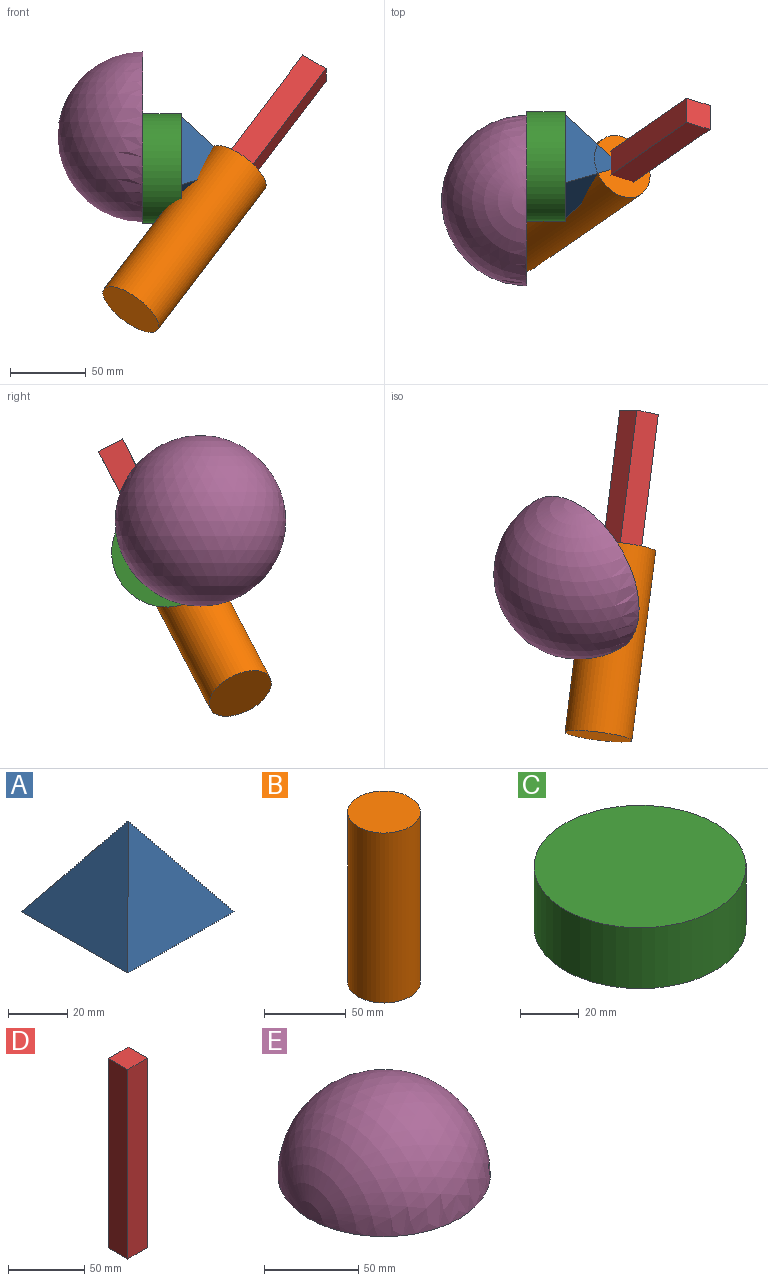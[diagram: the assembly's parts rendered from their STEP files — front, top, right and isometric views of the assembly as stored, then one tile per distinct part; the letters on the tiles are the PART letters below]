
ASSEMBLY  parts=5 mates=4
PART A: 5 faces, bbox 50.8x50.8x37.7 mm
  f0: plane 50.8x37.66mm, normal (-0.83,0,0.56), area 1153.7mm2, adj f1,f2,f3
  f1: plane 50.8x50.8mm, normal (0,0,-1), area 2580.6mm2, adj f0,f2,f3,f4
  f2: plane 50.8x37.66mm, normal (0,-0.83,0.56), area 1153.7mm2, adj f0,f1,f4
  f3: plane 50.8x37.66mm, normal (0,0.83,0.56), area 1153.7mm2, adj f0,f1,f4
  f4: plane 50.8x37.66mm, normal (0.83,0,0.56), area 1153.7mm2, adj f1,f2,f3
PART B: 3 faces, bbox 44.5x44.5x127 mm
  f0: cylinder r=22.26mm len=127mm, axis (0,0,-1), area 17763mm2, adj f1,f2
  f1: plane 44.52x44.52mm, normal (0,0,1), area 1556.7mm2, adj f0
  f2: plane 44.52x44.52mm, normal (0,0,-1), area 1556.7mm2, adj f0
PART C: 3 faces, bbox 72.4x72.4x25.4 mm
  f0: cylinder r=36.18mm len=72.36mm, axis (0,0,-1), area 5773.9mm2, adj f1,f2
  f1: plane 72.36x72.36mm, normal (0,0,1), area 4112.1mm2, adj f0
  f2: plane 72.36x72.36mm, normal (0,0,-1), area 4112.1mm2, adj f0
PART D: 6 faces, bbox 18.4x17.9x152.4 mm
  f0: plane 152.4x18.45mm, normal (0,1,0), area 2811.3mm2, adj f1,f3,f4,f5
  f1: plane 152.4x17.94mm, normal (-1,0,0), area 2734.1mm2, adj f0,f2,f4,f5
  f2: plane 152.4x18.45mm, normal (0,-1,0), area 2811.3mm2, adj f1,f3,f4,f5
  f3: plane 152.4x17.94mm, normal (1,0,0), area 2734.1mm2, adj f0,f2,f4,f5
  f4: plane 18.45x17.94mm, normal (0,0,1), area 330.9mm2, adj f0,f1,f2,f3
  f5: plane 18.45x17.94mm, normal (0,0,-1), area 330.9mm2, adj f0,f1,f2,f3
PART E: 2 faces, bbox 112.6x112.6x56.3 mm
  f0: sphere r=56.31mm, area 19922.9mm2, adj f1
  f1: plane 112.62x112.62mm, normal (0,0,-1), area 9961.5mm2, adj f0
PLACE A rot(axis=(0.46,0.76,0.46),105.6deg) t=(25.4,79.98,-12.31)mm
PLACE B rot(axis=(-0.62,0.77,-0.19),43.5deg) t=(-37.14,4.48,-108)mm
PLACE C rot(axis=(-0.54,0.65,-0.54),114.3deg) t=(0,22.54,-20.84)mm
PLACE D rot(axis=(0.95,-0.07,-0.29),153.6deg) t=(3.88,83.51,115.07)mm
PLACE E rot(axis=(-0.71,0,0.71),180deg) t=(0,-91.07,126.63)mm
MATE planar E.f1 <-> C.f0  axis (1,0,0) through (0,0,0)mm
MATE fastened A.f3 <-> B.f0  axis (0.56,0.38,0.73) through (63.06,22.54,-20.84)mm
MATE revolute A.f1 <-> C.f0  axis (-1,0,0) through (25.4,22.54,-20.84)mm
MATE slider D.f5 <-> B.f0  axis (0.56,0.38,0.73) through (113.48,57.19,45.4)mm
